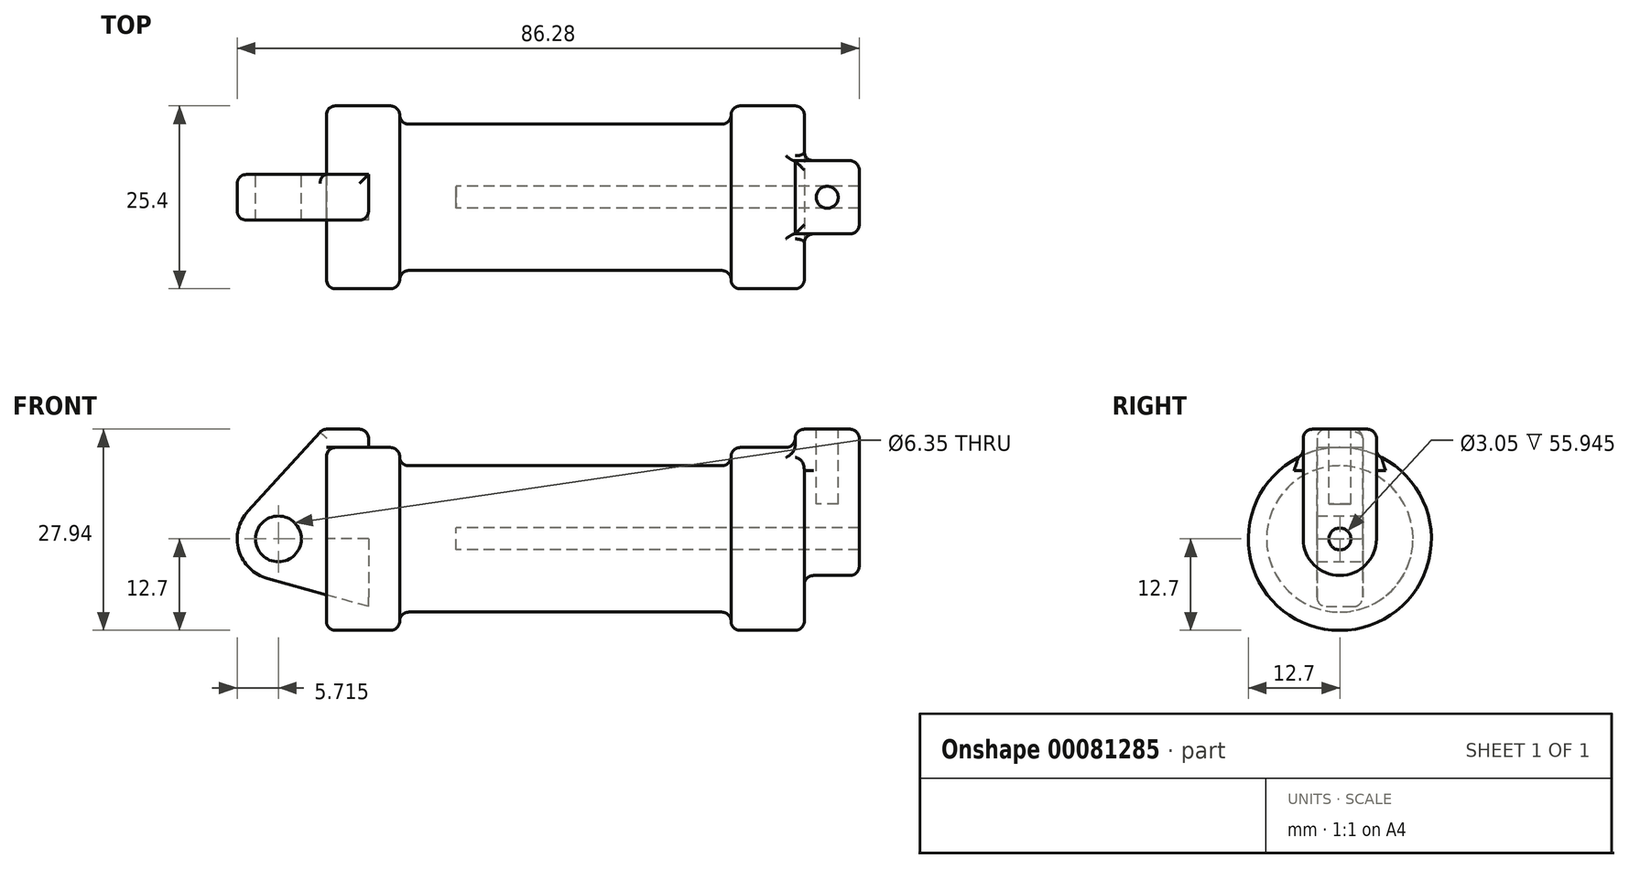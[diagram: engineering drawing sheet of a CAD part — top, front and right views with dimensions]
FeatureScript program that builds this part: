
annotation { "Feature Type Name" : "Feature", "Feature Type Description" : "" }
export const myFeature = defineFeature(function(context is Context, id is Id, definition is map)
    precondition{}
    {
        {
            var Q0;
            Q0=qCreatedBy(makeId("Front.planeOp"),FACE);
            var sketch = newSketch(context, id + "F0", { "sketchPlane" : qUnion([Q0])});
            skLineSegment(sketch, "E0", {"start": v(0, 0) * mm, "end": v(0, 12.7) * mm});
            skLineSegment(sketch, "E1", {"start": v(0, 12.7) * mm, "end": v(10.16, 12.7) * mm});
            skLineSegment(sketch, "E2", {"start": v(10.16, 12.7) * mm, "end": v(10.16, 10.16) * mm});
            skLineSegment(sketch, "E3", {"start": v(10.16, 10.16) * mm, "end": v(56.13, 10.16) * mm});
            skLineSegment(sketch, "E4", {"start": v(56.13, 10.16) * mm, "end": v(56.13, 12.7) * mm});
            skLineSegment(sketch, "E5", {"start": v(56.13, 12.7) * mm, "end": v(66.3, 12.7) * mm});
            skLineSegment(sketch, "E6", {"start": v(66.3, 12.7) * mm, "end": v(66.3, 0) * mm});
            skLineSegment(sketch, "E7", {"start": v(66.3, 0) * mm, "end": v(0, 0) * mm});
            skLineSegment(sketch, "E8", {"start": v(5.84, 15.24) * mm, "end": v(-0.5, 15.24) * mm});
            skLineSegment(sketch, "E9", {"start": v(-0.5, 15.24) * mm, "end": v(-10.88, 3.85) * mm});
            skLineSegment(sketch, "E10", {"start": v(0, 0) * mm, "end": v(-6.65, 0) * mm});
            skCircle(sketch, "E11", {"center": v(-6.65, 0) * mm, "radius": 5.72 * mm});
            skCircle(sketch, "E12", {"center": v(-6.65, 0) * mm, "radius": 3.18 * mm});
            skLineSegment(sketch, "E13", {"start": v(5.84, 15.24) * mm, "end": v(5.84, -9.4) * mm});
            skLineSegment(sketch, "E14", {"start": v(5.84, -9.4) * mm, "end": v(-8.18, -5.5) * mm});
            skSolve(sketch);
        }
        {
            var Q0;
            {var subQ0=sQuery(id+"F0.wireOp",EDGE,"E2");Q0=makeQuery(id+"F0.imprint","IMPRINT",FACE,{"disambiguationData":[TD([[makeQuery(id+"F0.imprint","IMPRINT",EDGE,{"derivedFrom":subQ0}),-1.0]])]});}
            var Q1;
            {var subQ0=sQuery(id+"F0.wireOp",EDGE,"E0");Q1=makeQuery(id+"F0.imprint","IMPRINT",FACE,{"disambiguationData":[TD([[makeQuery(id+"F0.imprint","IMPRINT",EDGE,{"derivedFrom":subQ0}),-1.0]])]});}
            var Q2;
            Q2=sQuery(id+"F0.wireOp",EDGE,"E7");
            revolve(context, id + "F1", {"entities" : qUnion([Q0, Q1]), "axis" : qUnion([Q2]), "revolveType" : RevolveType.FULL});
        }
        {
            var Q0;
            {var subQ3=sQuery(id+"F0.wireOp",EDGE,"E0");Q0=makeQuery(id+"F0.imprint","IMPRINT",FACE,{"disambiguationData":[TD([[makeQuery(id+"F0.imprint","IMPRINT",EDGE,{"derivedFrom":subQ3}),1.0]])]});}
            var Q1;
            {var subQ0=sQuery(id+"F0.wireOp",EDGE,"E14");Q1=makeQuery(id+"F0.imprint","IMPRINT",FACE,{"disambiguationData":[TD([[makeQuery(id+"F0.imprint","IMPRINT",EDGE,{"derivedFrom":subQ0}),-1.0]])]});}
            var Q2;
            {var subQ4=sQuery(id+"F0.wireOp",EDGE,"E12");Q2=makeQuery(id+"F0.imprint","IMPRINT",FACE,{"disambiguationData":[TD([[makeQuery(id+"F0.imprint","IMPRINT",EDGE,{"derivedFrom":subQ4}),-1.0]])]});}
            extrude(context, id + "F2", {"entities" : qUnion([Q0, Q1, Q2]), "endBound" : BoundingType.SYMMETRIC, "depth" : 6.35 * mm});
        }
        {
            var Q0;
            Q0=makeQuery(id+"F1.opRevolve","SWEPT_FACE",FACE,{"disambiguationData":[OSD([sQuery(id+"F0.wireOp",EDGE,"E6")])]});
            var sketch = newSketch(context, id + "F3", { "sketchPlane" : qUnion([Q0])});
            skCircle(sketch, "E15", {"center": v(0, 0) * mm, "radius": 5.08 * mm});
            skCircle(sketch, "E16", {"center": v(0, 0) * mm, "radius": 1.52 * mm});
            skLineSegment(sketch, "E17", {"start": v(-5.08, 0) * mm, "end": v(-5.08, 15.24) * mm});
            skLineSegment(sketch, "E18", {"start": v(5.08, 0) * mm, "end": v(5.08, 15.24) * mm});
            skLineSegment(sketch, "E19", {"start": v(5.08, 15.24) * mm, "end": v(-5.08, 15.24) * mm});
            skSolve(sketch);
        }
        {
            var Q0;
            {var subQ0=sQuery(id+"F3.wireOp",EDGE,"E17");var subQ1=sQuery(id+"F3.wireOp",EDGE,"E15");var subQ2=makeQuery(id+"F3.imprint","INTERSECT",VERTEX,{"derivedFrom":[subQ1,subQ0]});Q0=makeQuery(id+"F3.imprint","IMPRINT",FACE,{"disambiguationData":[TD([[makeQuery(id+"F3.imprint","IMPRINT",EDGE,{"disambiguationData":[TD([[subQ2,1.0]])],"derivedFrom":subQ1}),-1.0]])]});}
            var Q1;
            {var subQ0=sQuery(id+"F3.wireOp",EDGE,"E19");Q1=makeQuery(id+"F3.imprint","IMPRINT",FACE,{"disambiguationData":[TD([[makeQuery(id+"F3.imprint","IMPRINT",EDGE,{"derivedFrom":subQ0}),1.0]])]});}
            var Q2;
            Q2=makeQuery(id+"F3.imprint","IMPRINT",FACE,{"disambiguationData":[TD([[makeQuery(id+"F3.imprint","IMPRINT",EDGE,{"derivedFrom":sQuery(id+"F3.wireOp",EDGE,"E16")}),-1.0]])]});
            extrude(context, id + "F4", {"entities" : qUnion([Q0, Q1, Q2]), "operationType" : NewBodyOperationType.ADD, "depth" : 7.62 * mm, "hasSecondDirection" : true, "secondDirectionOppositeDirection" : true, "secondDirectionDepth" : 1.27 * mm});
        }
        {
            var Q0;
            Q0=makeQuery(id+"F4.opExtrude","CAP_FACE",FACE,{"disambiguationData":[OSD([sQuery(id+"F3.wireOp",EDGE,"E15"),sQuery(id+"F3.wireOp",EDGE,"E16"),sQuery(id+"F3.wireOp",EDGE,"E17"),sQuery(id+"F3.wireOp",EDGE,"E18"),sQuery(id+"F3.wireOp",EDGE,"E19")])],"isStart":false});
            var sketch = newSketch(context, id + "F5", { "sketchPlane" : qUnion([Q0])});
            skCircle(sketch, "E20", {"center": v(0, 0) * mm, "radius": 1.52 * mm});
            skSolve(sketch);
        }
        {
            var Q0;
            Q0=makeQuery(id+"F5.imprint","IMPRINT",FACE,{"disambiguationData":[TD([[makeQuery(id+"F5.imprint","IMPRINT",EDGE,{"derivedFrom":sQuery(id+"F5.wireOp",EDGE,"E20")}),1.0]])]});
            var Q1;
            Q1=sQuery(id+"F5.wireOp",EDGE,"E20");
            extrude(context, id + "F6", {"entities" : qUnion([Q0]), "operationType" : NewBodyOperationType.REMOVE, "surfaceEntities" : qUnion([Q1]), "oppositeDirection" : true, "depth" : 55.94 * mm});
        }
        {
            var Q0;
            Q0=makeQuery(id+"F2.opExtrude","SWEPT_FACE",FACE,{"disambiguationData":[OSD([sQuery(id+"F0.wireOp",EDGE,"E8")])]});
            var sketch = newSketch(context, id + "F7", { "sketchPlane" : qUnion([Q0])});
            skCircle(sketch, "E21", {"center": v(2.67, 0) * mm, "radius": 1.52 * mm});
            skPoint(sketch, "E21.centerSnap0", {"position": v(2.67, 3.18) * mm});
            skPoint(sketch, "E21.centerSnap1", {"position": v(-0.5, 0) * mm});
            skSolve(sketch);
        }
        {
            var Q0;
            Q0=makeQuery(id+"F4.opExtrude","SWEPT_FACE",FACE,{"disambiguationData":[OSD([sQuery(id+"F3.wireOp",EDGE,"E19")])]});
            var sketch = newSketch(context, id + "F8", { "sketchPlane" : qUnion([Q0])});
            skCircle(sketch, "E22", {"center": v(69.47, 0) * mm, "radius": 1.52 * mm});
            skPoint(sketch, "E22.centerSnap0", {"position": v(65.02, 0) * mm});
            skPoint(sketch, "E22.centerSnap1", {"position": v(69.47, 5.08) * mm});
            skSolve(sketch);
        }
        {
            var Q0;
            Q0=makeQuery(id+"F8.imprint","IMPRINT",FACE,{"disambiguationData":[TD([[makeQuery(id+"F8.imprint","IMPRINT",EDGE,{"derivedFrom":sQuery(id+"F8.wireOp",EDGE,"E22")}),1.0]])]});
            extrude(context, id + "F9", {"entities" : qUnion([Q0]), "oppositeDirection" : true, "depth" : 10.4 * mm});
        }
        {
            var Q0;
            Q0=sQuery(id+"F7.wireOp",EDGE,"E21");
            extrude(context, id + "F10", {"bodyType" : ToolBodyType.SURFACE, "surfaceEntities" : qUnion([Q0]), "oppositeDirection" : true, "depth" : 17.78 * mm});
        }
        {
            var Q0;
            Q0=makeQuery(id+"F1.opRevolve","SWEPT_FACE",FACE,{"disambiguationData":[OSD([sQuery(id+"F0.wireOp",EDGE,"E1")])]});
            var Q1;
            Q1=makeQuery(id+"F1.opRevolve","SWEPT_EDGE",EDGE,{"disambiguationData":[OSD([sQuery(id+"F0.wireOp",EDGE,"E4"),sQuery(id+"F0.wireOp",EDGE,"E5")])]});
            var Q2;
            Q2=makeQuery(id+"F1.opRevolve","SWEPT_EDGE",EDGE,{"disambiguationData":[OSD([sQuery(id+"F0.wireOp",EDGE,"E3"),sQuery(id+"F0.wireOp",EDGE,"E4")])]});
            var Q3;
            Q3=makeQuery(id+"F1.opRevolve","SWEPT_EDGE",EDGE,{"disambiguationData":[OSD([sQuery(id+"F0.wireOp",EDGE,"E5"),sQuery(id+"F0.wireOp",EDGE,"E6")])]});
            var Q4;
            Q4=makeQuery(id+"F1.opRevolve","SWEPT_EDGE",EDGE,{"disambiguationData":[OSD([sQuery(id+"F0.wireOp",EDGE,"E2"),sQuery(id+"F0.wireOp",EDGE,"E3")])]});
            fillet(context, id + "F11", {"entities" : qUnion([Q0, Q1, Q2, Q3, Q4]), "radius" : 1.27 * mm, "tangentPropagation" : true, "allowEdgeOverflow" : false});
        }
        {
            var Q0;
            Q0=makeQuery(id+"F4.boolean.opBoolean","INTERSECT",EDGE,{"derivedFrom":[makeQuery(id+"F1.opRevolve","SWEPT_FACE",FACE,{"disambiguationData":[OSD([sQuery(id+"F0.wireOp",EDGE,"E6")])]}),makeQuery(id+"F4.opExtrude","SWEPT_FACE",FACE,{"disambiguationData":[OSD([sQuery(id+"F3.wireOp",EDGE,"E17")])]})]});
            var Q1;
            Q1=makeQuery(id+"F4.opExtrude","CAP_EDGE",EDGE,{"disambiguationData":[OSD([sQuery(id+"F3.wireOp",EDGE,"E17")])],"isStart":false});
            var Q2;
            Q2=makeQuery(id+"F4.opExtrude","SWEPT_EDGE",EDGE,{"disambiguationData":[OSD([sQuery(id+"F3.wireOp",EDGE,"E17"),sQuery(id+"F3.wireOp",EDGE,"E19")])]});
            var Q3;
            Q3=makeQuery(id+"F4.opExtrude","CAP_EDGE",EDGE,{"disambiguationData":[OSD([sQuery(id+"F3.wireOp",EDGE,"E19")])],"isStart":false});
            var Q4;
            Q4=makeQuery(id+"F4.opExtrude","SWEPT_EDGE",EDGE,{"disambiguationData":[OSD([sQuery(id+"F3.wireOp",EDGE,"E18"),sQuery(id+"F3.wireOp",EDGE,"E19")])]});
            var Q5;
            Q5=makeQuery(id+"F4.opExtrude","CAP_EDGE",EDGE,{"disambiguationData":[OSD([sQuery(id+"F3.wireOp",EDGE,"E19")])],"isStart":true});
            var Q6;
            Q6=makeQuery(id+"F4.boolean.opBoolean","INTERSECT",EDGE,{"derivedFrom":[makeQuery(id+"F1.opRevolve","SWEPT_FACE",FACE,{"disambiguationData":[OSD([sQuery(id+"F0.wireOp",EDGE,"E5")])]}),makeQuery(id+"F4.opExtrude","CAP_FACE",FACE,{"disambiguationData":[OSD([sQuery(id+"F3.wireOp",EDGE,"E15"),sQuery(id+"F3.wireOp",EDGE,"E16"),sQuery(id+"F3.wireOp",EDGE,"E17"),sQuery(id+"F3.wireOp",EDGE,"E18"),sQuery(id+"F3.wireOp",EDGE,"E19")])],"isStart":true})]});
            fillet(context, id + "F12", {"entities" : qUnion([Q0, Q1, Q2, Q3, Q4, Q5, Q6]), "radius" : 1.27 * mm, "tangentPropagation" : true, "allowEdgeOverflow" : false});
        }
        {
            var Q0;
            Q0=makeQuery(id+"F2.opExtrude","CAP_EDGE",EDGE,{"disambiguationData":[OSD([sQuery(id+"F0.wireOp",EDGE,"E9")])],"isStart":false});
            var Q1;
            Q1=makeQuery(id+"F2.opExtrude","CAP_EDGE",EDGE,{"disambiguationData":[OSD([sQuery(id+"F0.wireOp",EDGE,"E11")])],"isStart":false});
            var Q2;
            Q2=makeQuery(id+"F2.opExtrude","CAP_EDGE",EDGE,{"disambiguationData":[OSD([sQuery(id+"F0.wireOp",EDGE,"E14")])],"isStart":false});
            var Q3;
            {var subQ0=sQuery(id+"F0.wireOp",EDGE,"E13");Q3=makeQuery(id+"F2.opExtrude","CAP_EDGE",EDGE,{"disambiguationData":[OSD([subQ0]),TDD([makeQuery(id+"F0.imprint","IMPRINT",EDGE,{"disambiguationData":[TD([[makeQuery(id+"F0.imprint","INTERSECT",VERTEX,{"derivedFrom":[sQuery(id+"F0.wireOp",EDGE,"E8"),subQ0]}),-1.0]])],"derivedFrom":subQ0})])],"isStart":false});}
            var Q4;
            Q4=makeQuery(id+"F2.opExtrude","SWEPT_EDGE",EDGE,{"disambiguationData":[OSD([sQuery(id+"F0.wireOp",EDGE,"E8"),sQuery(id+"F0.wireOp",EDGE,"E13")])]});
            var Q5;
            Q5=makeQuery(id+"F2.opExtrude","CAP_EDGE",EDGE,{"disambiguationData":[OSD([sQuery(id+"F0.wireOp",EDGE,"E8")])],"isStart":true});
            var Q6;
            Q6=makeQuery(id+"F2.opExtrude","SWEPT_EDGE",EDGE,{"disambiguationData":[OSD([sQuery(id+"F0.wireOp",EDGE,"E8"),sQuery(id+"F0.wireOp",EDGE,"E9")])]});
            var Q7;
            Q7=makeQuery(id+"F2.opExtrude","CAP_EDGE",EDGE,{"disambiguationData":[OSD([sQuery(id+"F0.wireOp",EDGE,"E8")])],"isStart":false});
            fillet(context, id + "F13", {"entities" : qUnion([Q0, Q1, Q2, Q3, Q4, Q5, Q6, Q7]), "radius" : 1.27 * mm, "tangentPropagation" : true, "allowEdgeOverflow" : false});
        }
        {
            var Q0;
            Q0=makeQuery(id+"F2.opExtrude","CAP_EDGE",EDGE,{"disambiguationData":[OSD([sQuery(id+"F0.wireOp",EDGE,"E9")])],"isStart":true});
            fillet(context, id + "F14", {"entities" : qUnion([Q0]), "radius" : 1.27 * mm, "tangentPropagation" : true, "allowEdgeOverflow" : false});
        }
    });
